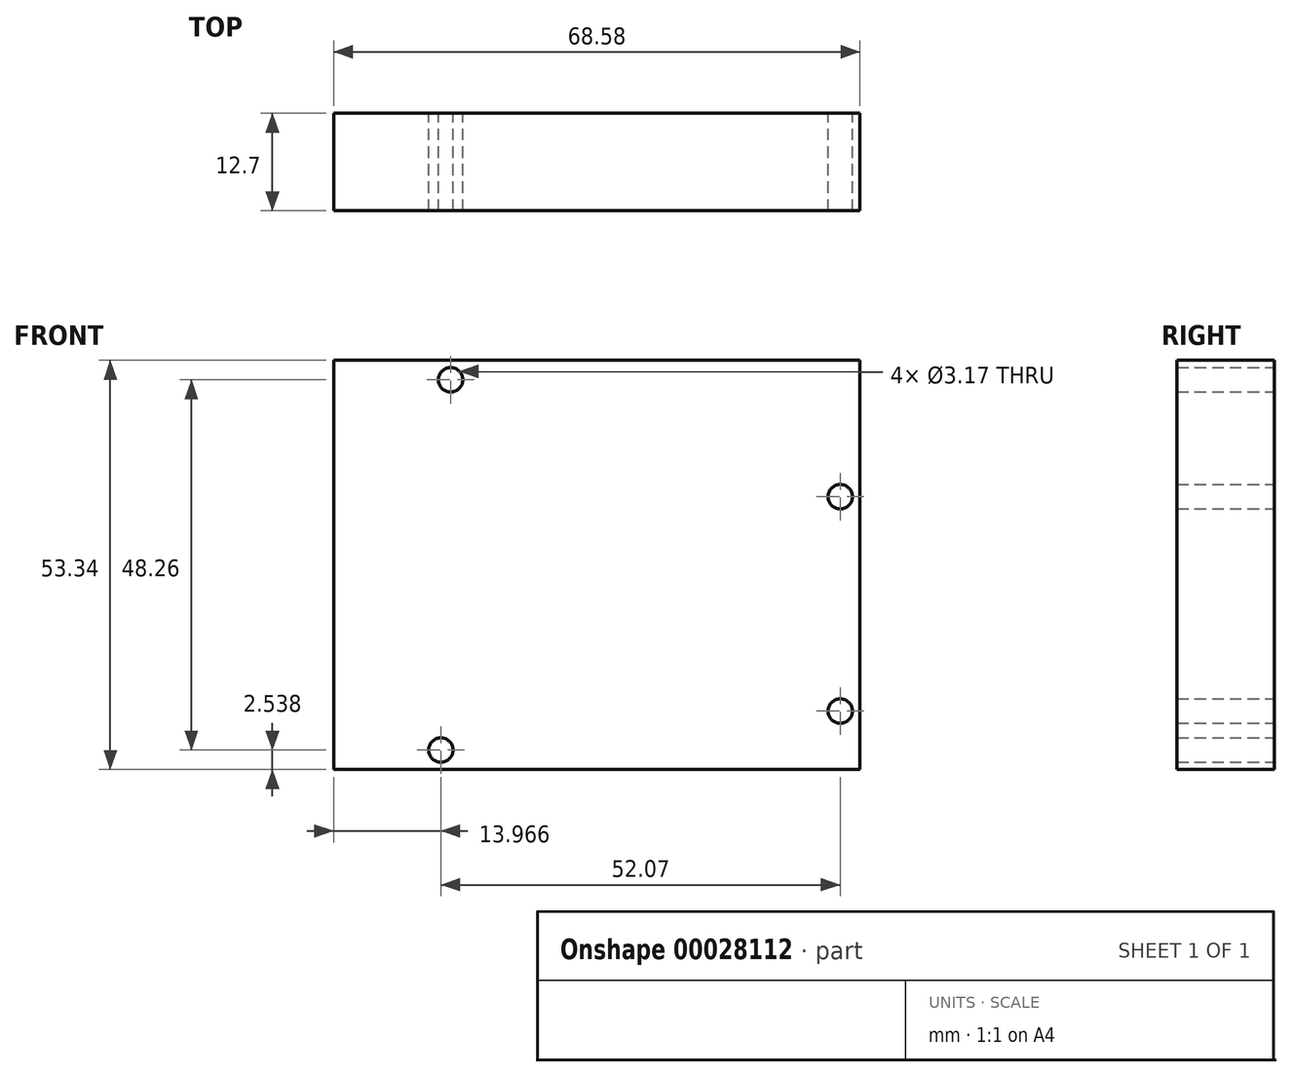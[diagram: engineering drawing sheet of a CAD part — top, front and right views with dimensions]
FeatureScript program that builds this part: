
annotation { "Feature Type Name" : "Feature", "Feature Type Description" : "" }
export const myFeature = defineFeature(function(context is Context, id is Id, definition is map)
    precondition{}
    {
        {
            var Q0;
            Q0=qCreatedBy(makeId("Front.planeOp"),FACE);
            var sketch = newSketch(context, id + "F0", { "sketchPlane" : qUnion([Q0])});
            skCircle(sketch, "E0", {"center": v(11.1, 18.37) * mm, "radius": 1.59 * mm});
            skLineSegment(sketch, "E1", {"start": v(11.1, 18.37) * mm, "end": v(11.1, -9.57) * mm, "construction": true});
            skCircle(sketch, "E2", {"center": v(11.1, -9.57) * mm, "radius": 1.59 * mm});
            skLineSegment(sketch, "E3", {"start": v(11.1, -9.57) * mm, "end": v(11.1, -14.65) * mm, "construction": true});
            skLineSegment(sketch, "E4", {"start": v(11.1, -14.65) * mm, "end": v(-40.96, -14.65) * mm, "construction": true});
            skCircle(sketch, "E5", {"center": v(-40.96, -14.65) * mm, "radius": 1.59 * mm});
            skLineSegment(sketch, "E6", {"start": v(11.1, 18.37) * mm, "end": v(11.1, 33.6) * mm, "construction": true});
            skLineSegment(sketch, "E7", {"start": v(11.1, 33.6) * mm, "end": v(-39.7, 33.6) * mm, "construction": true});
            skCircle(sketch, "E8", {"center": v(-39.7, 33.6) * mm, "radius": 1.59 * mm});
            skLineSegment(sketch, "E9.bottom", {"start": v(-54.93, -17.2) * mm, "end": v(13.65, -17.2) * mm});
            skLineSegment(sketch, "E9.top", {"start": v(-54.93, 36.15) * mm, "end": v(13.65, 36.15) * mm});
            skLineSegment(sketch, "E9.left", {"start": v(-54.93, -17.2) * mm, "end": v(-54.93, 36.15) * mm});
            skLineSegment(sketch, "E9.right", {"start": v(13.65, -17.2) * mm, "end": v(13.65, 36.15) * mm});
            skLineSegment(sketch, "E10", {"start": v(11.1, -14.65) * mm, "end": v(11.1, -17.2) * mm, "construction": true});
            skLineSegment(sketch, "E11", {"start": v(-40.96, -14.65) * mm, "end": v(-54.93, -14.65) * mm, "construction": true});
            skLineSegment(sketch, "E12", {"start": v(-54.93, -14.65) * mm, "end": v(-54.93, -17.2) * mm, "construction": true});
            skLineSegment(sketch, "E13", {"start": v(-54.93, -17.2) * mm, "end": v(11.1, -17.2) * mm, "construction": true});
            skSolve(sketch);
        }
        {
            var Q0;
            Q0=makeQuery(id+"F0.imprint","IMPRINT",FACE,{"disambiguationData":[TD([[makeQuery(id+"F0.imprint","IMPRINT",EDGE,{"derivedFrom":sQuery(id+"F0.wireOp",EDGE,"E0")}),-1.0]])]});
            extrude(context, id + "F1", {"entities" : qUnion([Q0]), "depth" : 12.7 * mm});
        }
    });
